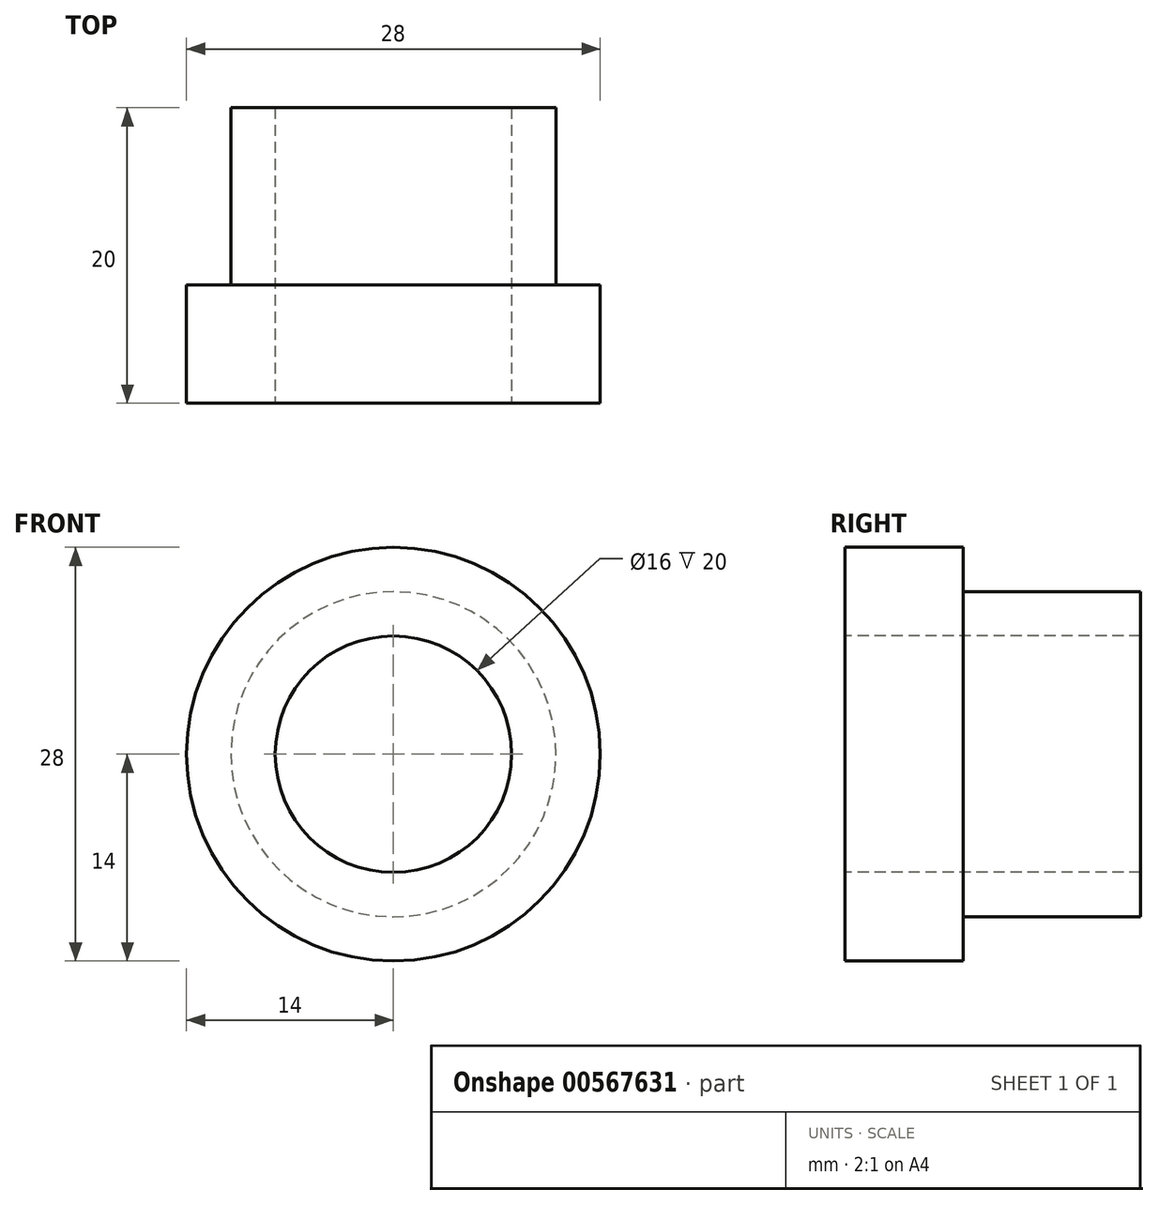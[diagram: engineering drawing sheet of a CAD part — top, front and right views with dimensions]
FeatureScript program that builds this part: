
annotation { "Feature Type Name" : "Feature", "Feature Type Description" : "" }
export const myFeature = defineFeature(function(context is Context, id is Id, definition is map)
    precondition{}
    {
        {
            var Q0;
            Q0=qCreatedBy(makeId("Front.planeOp"),FACE);
            var sketch = newSketch(context, id + "F0", { "sketchPlane" : qUnion([Q0])});
            skCircle(sketch, "E0", {"center": v(0, 0) * mm, "radius": 8 * mm});
            skCircle(sketch, "E1", {"center": v(0, 0) * mm, "radius": 11 * mm});
            skCircle(sketch, "E2", {"center": v(0, 0) * mm, "radius": 14 * mm});
            skSolve(sketch);
        }
        {
            var Q0;
            Q0=makeQuery(id+"F0.imprint","IMPRINT",FACE,{"disambiguationData":[TD([[makeQuery(id+"F0.imprint","IMPRINT",EDGE,{"derivedFrom":sQuery(id+"F0.wireOp",EDGE,"E1")}),-1.0]])]});
            var Q1;
            Q1=makeQuery(id+"F0.imprint","IMPRINT",FACE,{"disambiguationData":[TD([[makeQuery(id+"F0.imprint","IMPRINT",EDGE,{"derivedFrom":sQuery(id+"F0.wireOp",EDGE,"E0")}),-1.0]])]});
            extrude(context, id + "F1", {"entities" : qUnion([Q0, Q1]), "oppositeDirection" : true, "depth" : 8 * mm, "offsetDistance" : 25.4 * mm});
        }
        {
            var Q0;
            Q0=makeQuery(id+"F0.imprint","IMPRINT",FACE,{"disambiguationData":[TD([[makeQuery(id+"F0.imprint","IMPRINT",EDGE,{"derivedFrom":sQuery(id+"F0.wireOp",EDGE,"E0")}),-1.0]])]});
            extrude(context, id + "F2", {"entities" : qUnion([Q0]), "operationType" : NewBodyOperationType.ADD, "oppositeDirection" : true, "depth" : 20 * mm, "offsetDistance" : 25.4 * mm});
        }
    });
